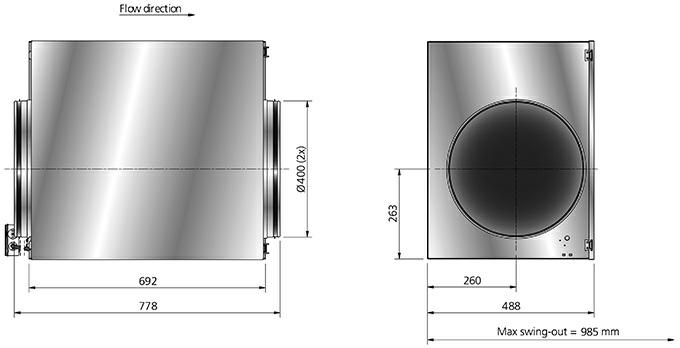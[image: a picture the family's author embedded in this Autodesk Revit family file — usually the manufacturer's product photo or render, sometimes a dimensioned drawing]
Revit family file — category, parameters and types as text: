
# Revit family: IRE 400 F3 ErP AC_
name_source: partatom
category: Mechanical Equipment
revit_build: Autodesk Revit MEP 2014 (Build: 20130308_1515(x64)
units: mm (PartAtom-declared; Revit-internal decimal feet)

## types (1)
- IRE 400 F3 ErP AC
    Capacitor = - μF
    Current = 3 A
    Depth = 642 mm  [stored 2.1063 ft]
    Description = Insulated duct fans with circular connections
    Diameter = 400 mm  [stored 1.31234 ft]
    Frequency = 50 Hz
    Height = 488 mm  [stored 1.60105 ft]
    Main Material = Steel, Galvanized
    Max. temperature of transported air = 45 °C
    Max. temperature of transported air when speed controlled = 45 °C
    Phase = 3
    Power = 1470 W
    Sound pressure level at 3 m = 50 dB(A)
    Speed = 1310 rpm
    Voltage = 400 V
    Voltage range = 380-415 V
    Weight = 46.50 kg
    Width = 778 mm  [stored 2.55249 ft]
    Wiring diagram = Y 4040004 / Δ 4040003

note: [stored X ft] marks values corroborated as IEEE doubles in the binary element streams (Revit-internal decimal feet)

## geometry (parser evidence)
native form markers: Sweep x5
no freeform markers — native parametric forms only
